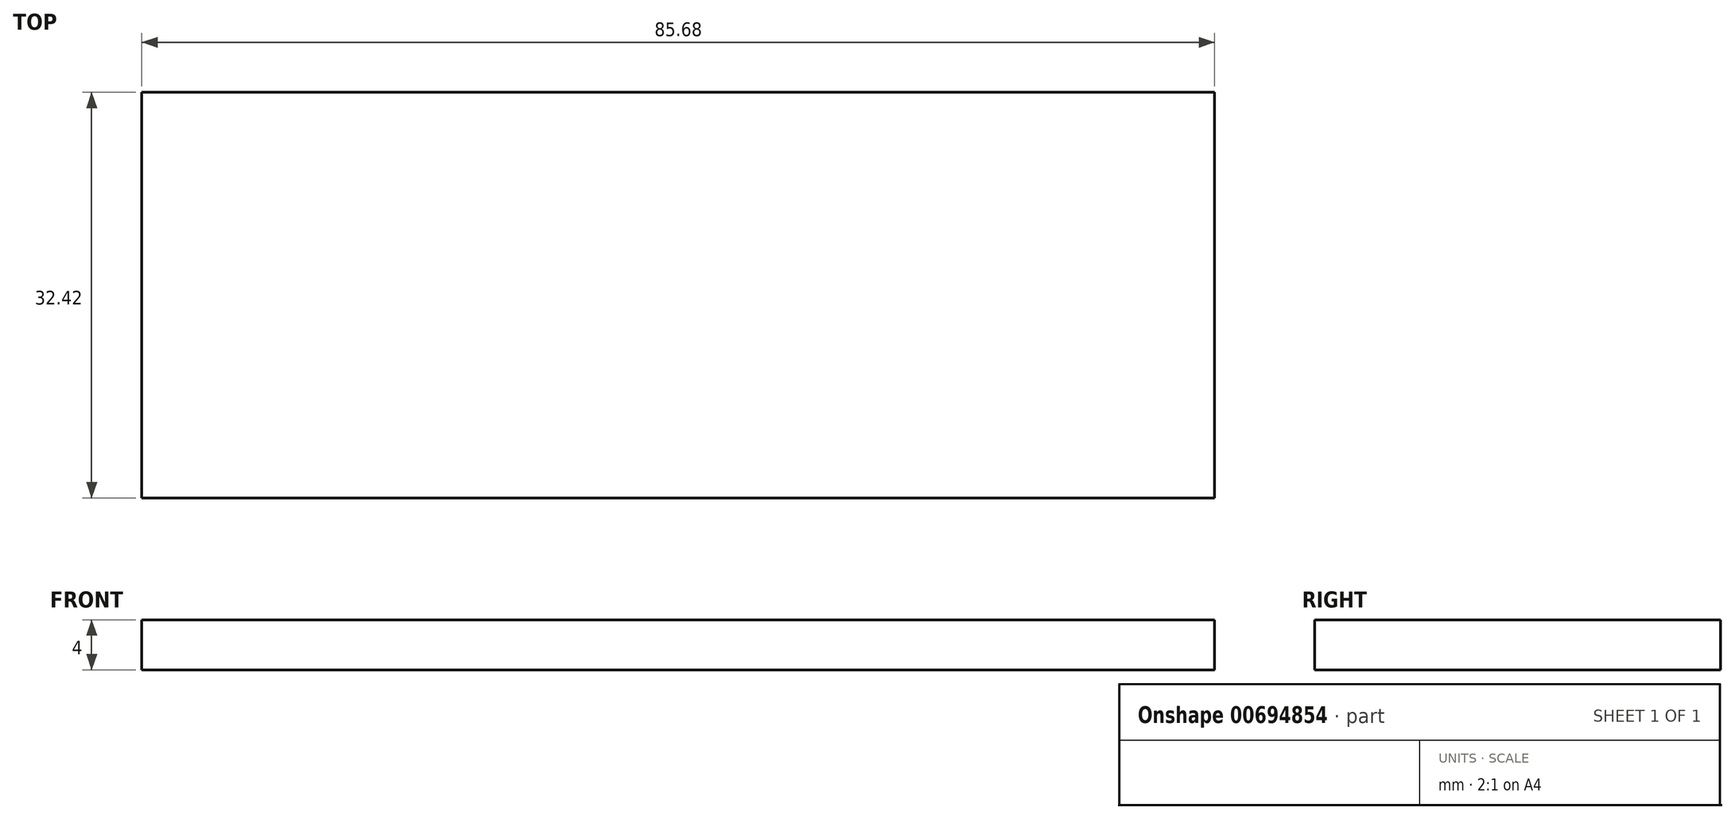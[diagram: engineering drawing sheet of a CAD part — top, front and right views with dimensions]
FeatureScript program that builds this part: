
annotation { "Feature Type Name" : "Feature", "Feature Type Description" : "" }
export const myFeature = defineFeature(function(context is Context, id is Id, definition is map)
    precondition{}
    {
        {
            var Q0;
            Q0=qCreatedBy(makeId("Top.planeOp"),FACE);
            var sketch = newSketch(context, id + "F0", { "sketchPlane" : qUnion([Q0])});
            skLineSegment(sketch, "E0.bottom", {"start": v(0, 0) * mm, "end": v(85.68, 0) * mm});
            skLineSegment(sketch, "E0.top", {"start": v(0, -32.42) * mm, "end": v(85.68, -32.42) * mm});
            skLineSegment(sketch, "E0.left", {"start": v(0, 0) * mm, "end": v(0, -32.42) * mm});
            skLineSegment(sketch, "E0.right", {"start": v(85.68, 0) * mm, "end": v(85.68, -32.42) * mm});
            skSolve(sketch);
        }
        {
            var Q0;
            Q0=qSketchRegion(id+"F0",true);
            extrude(context, id + "F1", {"entities" : qUnion([Q0]), "depth" : 4 * mm, "offsetDistance" : 25.4 * mm});
        }
    });
